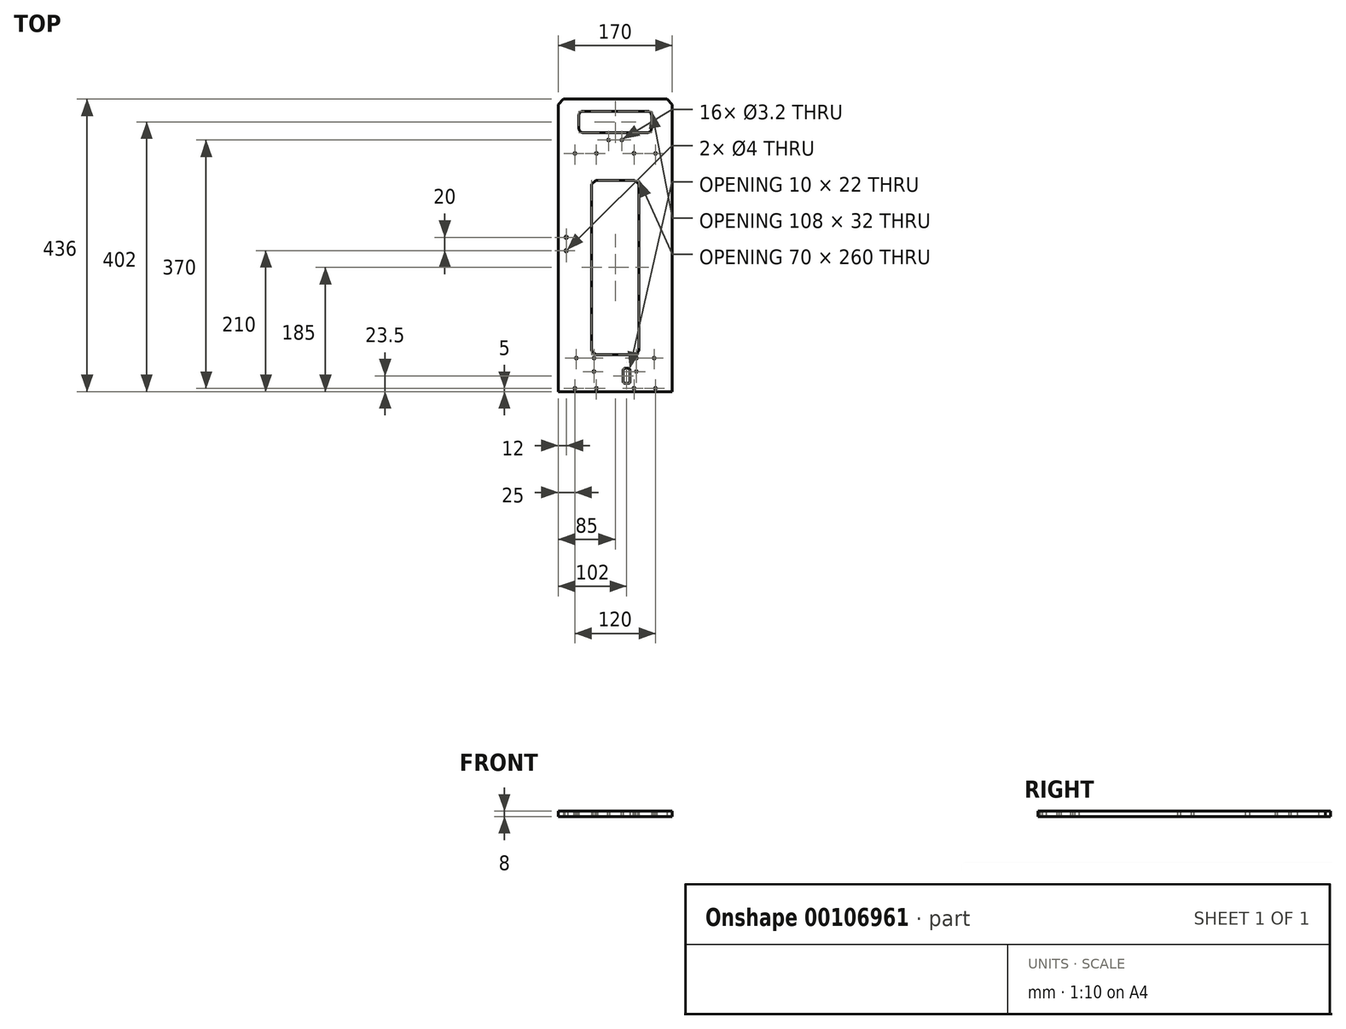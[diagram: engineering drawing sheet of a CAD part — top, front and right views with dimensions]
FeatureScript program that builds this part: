
annotation { "Feature Type Name" : "Feature", "Feature Type Description" : "" }
export const myFeature = defineFeature(function(context is Context, id is Id, definition is map)
    precondition{}
    {
        {
            var Q0;
            Q0=qCreatedBy(makeId("Top.planeOp"),FACE);
            var sketch = newSketch(context, id + "F0", { "sketchPlane" : qUnion([Q0])});
            skLineSegment(sketch, "E0", {"start": v(85, 210) * mm, "end": v(85, -218) * mm});
            skLineSegment(sketch, "E1", {"start": v(85, 210) * mm, "end": v(77, 218) * mm});
            skLineSegment(sketch, "E2", {"start": v(85, -218) * mm, "end": v(-85, -218) * mm});
            skLineSegment(sketch, "E3", {"start": v(-77, 218) * mm, "end": v(77, 218) * mm});
            skLineSegment(sketch, "E4", {"start": v(-85, -218) * mm, "end": v(-85, 210) * mm});
            skLineSegment(sketch, "E5", {"start": v(-85, 210) * mm, "end": v(-77, 218) * mm});
            skCircle(sketch, "E6", {"center": v(-31.5, -168) * mm, "radius": 1.6 * mm});
            skCircle(sketch, "E7", {"center": v(-31.5, -188) * mm, "radius": 1.6 * mm});
            skCircle(sketch, "E8", {"center": v(31.5, -188) * mm, "radius": 1.6 * mm});
            skCircle(sketch, "E9", {"center": v(31.5, -168) * mm, "radius": 1.6 * mm});
            skArc(sketch, "E10", {"start": v(14, -183.5) * mm, "mid": v(12.59, -184.09) * mm, "end": v(12, -185.5) * mm});
            skLineSegment(sketch, "E11", {"start": v(14, -183.5) * mm, "end": v(20, -183.5) * mm});
            skLineSegment(sketch, "E12", {"start": v(12, -203.5) * mm, "end": v(12, -185.5) * mm});
            skArc(sketch, "E13", {"start": v(22, -185.5) * mm, "mid": v(21.41, -184.09) * mm, "end": v(20, -183.5) * mm});
            skArc(sketch, "E14", {"start": v(12, -203.5) * mm, "mid": v(12.59, -204.91) * mm, "end": v(14, -205.5) * mm});
            skLineSegment(sketch, "E15", {"start": v(22, -185.5) * mm, "end": v(22, -203.5) * mm});
            skLineSegment(sketch, "E16", {"start": v(20, -205.5) * mm, "end": v(14, -205.5) * mm});
            skArc(sketch, "E17", {"start": v(20, -205.5) * mm, "mid": v(21.41, -204.91) * mm, "end": v(22, -203.5) * mm});
            skCircle(sketch, "E18", {"center": v(-58, -168) * mm, "radius": 1.6 * mm});
            skCircle(sketch, "E19", {"center": v(-73, -8) * mm, "radius": 2 * mm});
            skCircle(sketch, "E20", {"center": v(-73, 12) * mm, "radius": 2 * mm});
            skLineSegment(sketch, "E21", {"start": v(-29, 97) * mm, "end": v(29, 97) * mm});
            skLineSegment(sketch, "E22", {"start": v(-29, 97) * mm, "end": v(-35, 91) * mm});
            skLineSegment(sketch, "E23", {"start": v(29, 97) * mm, "end": v(35, 91) * mm});
            skLineSegment(sketch, "E24", {"start": v(-35, -157) * mm, "end": v(-35, 91) * mm});
            skLineSegment(sketch, "E25", {"start": v(35, 91) * mm, "end": v(35, -157) * mm});
            skLineSegment(sketch, "E26", {"start": v(-29, -163) * mm, "end": v(-35, -157) * mm});
            skLineSegment(sketch, "E27", {"start": v(35, -157) * mm, "end": v(29, -163) * mm});
            skLineSegment(sketch, "E28", {"start": v(29, -163) * mm, "end": v(-29, -163) * mm});
            skCircle(sketch, "E29", {"center": v(60, 137) * mm, "radius": 1.6 * mm});
            skCircle(sketch, "E30", {"center": v(58, -168) * mm, "radius": 1.6 * mm});
            skCircle(sketch, "E31", {"center": v(-60, 137) * mm, "radius": 1.6 * mm});
            skCircle(sketch, "E32", {"center": v(-28, 137) * mm, "radius": 1.6 * mm});
            skCircle(sketch, "E33", {"center": v(28, 137) * mm, "radius": 1.6 * mm});
            skCircle(sketch, "E34", {"center": v(60, -213) * mm, "radius": 1.6 * mm});
            skCircle(sketch, "E35", {"center": v(28, -213) * mm, "radius": 1.6 * mm});
            skCircle(sketch, "E36", {"center": v(-28, -213) * mm, "radius": 1.6 * mm});
            skCircle(sketch, "E37", {"center": v(-60, -213) * mm, "radius": 1.6 * mm});
            skCircle(sketch, "E38", {"center": v(10, 157) * mm, "radius": 1.6 * mm});
            skCircle(sketch, "E39", {"center": v(-10, 157) * mm, "radius": 1.6 * mm});
            skArc(sketch, "E40", {"start": v(-48, 200) * mm, "mid": v(-52.24, 198.24) * mm, "end": v(-54, 194) * mm});
            skLineSegment(sketch, "E41", {"start": v(-54, 174) * mm, "end": v(-54, 194) * mm});
            skArc(sketch, "E42", {"start": v(-54, 174) * mm, "mid": v(-52.24, 169.76) * mm, "end": v(-48, 168) * mm});
            skLineSegment(sketch, "E43", {"start": v(48, 168) * mm, "end": v(-48, 168) * mm});
            skArc(sketch, "E44", {"start": v(48, 168) * mm, "mid": v(52.24, 169.76) * mm, "end": v(54, 174) * mm});
            skLineSegment(sketch, "E45", {"start": v(54, 194) * mm, "end": v(54, 174) * mm});
            skArc(sketch, "E46", {"start": v(54, 194) * mm, "mid": v(52.24, 198.24) * mm, "end": v(48, 200) * mm});
            skLineSegment(sketch, "E47", {"start": v(-48, 200) * mm, "end": v(48, 200) * mm});
            skSolve(sketch);
        }
        {
            var Q0;
            Q0 = qSketchRegion(id + "F0", true);
            extrude(context, id + "F1", {"entities" : qUnion([Q0]), "depth" : 8 * mm});
        }
    });
